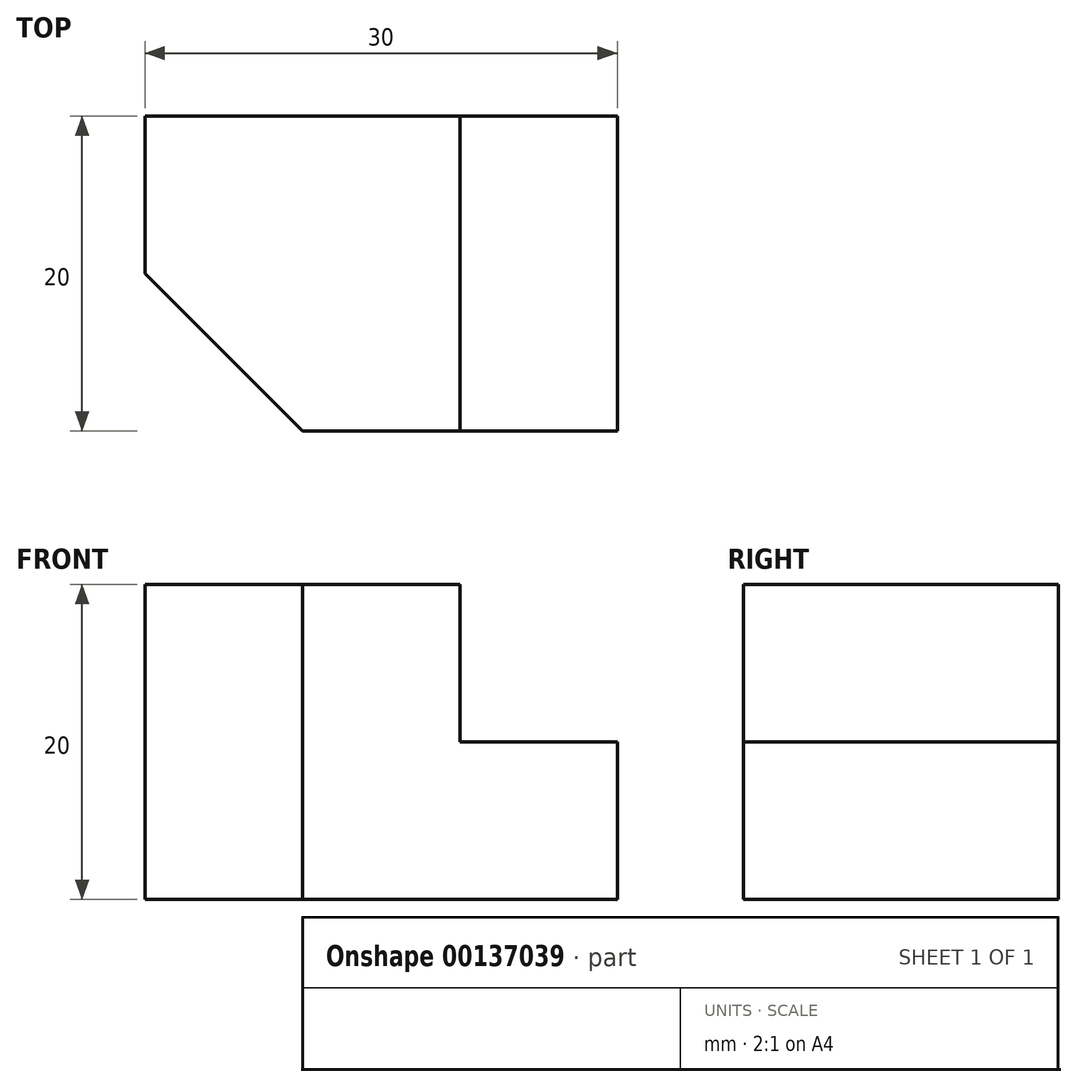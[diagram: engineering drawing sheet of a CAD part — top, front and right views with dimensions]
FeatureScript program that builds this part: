
annotation { "Feature Type Name" : "Feature", "Feature Type Description" : "" }
export const myFeature = defineFeature(function(context is Context, id is Id, definition is map)
    precondition{}
    {
        {
            var Q0;
            Q0=qCreatedBy(makeId("Top.planeOp"),FACE);
            var sketch = newSketch(context, id + "F0", { "sketchPlane" : qUnion([Q0])});
            skLineSegment(sketch, "E0.bottom", {"start": v(0, 0) * mm, "end": v(30, 0) * mm});
            skLineSegment(sketch, "E0.top", {"start": v(0, 20) * mm, "end": v(30, 20) * mm});
            skLineSegment(sketch, "E0.left", {"start": v(0, 0) * mm, "end": v(0, 20) * mm});
            skLineSegment(sketch, "E0.right", {"start": v(30, 0) * mm, "end": v(30, 20) * mm});
            skSolve(sketch);
        }
        {
            var Q0;
            Q0 = qSketchRegion(id + "F0", true);
            extrude(context, id + "F1", {"entities" : qUnion([Q0]), "depth" : 20 * mm});
        }
        {
            var Q0;
            Q0=makeQuery(id+"F1.opExtrude","CAP_FACE",FACE,{"disambiguationData":[OSD([sQuery(id+"F0.wireOp",EDGE,"E0.bottom"),sQuery(id+"F0.wireOp",EDGE,"E0.top"),sQuery(id+"F0.wireOp",EDGE,"E0.left"),sQuery(id+"F0.wireOp",EDGE,"E0.right")])],"isStart":false});
            var sketch = newSketch(context, id + "F2", { "sketchPlane" : qUnion([Q0])});
            skLineSegment(sketch, "E1.bottom", {"start": v(30, 20) * mm, "end": v(20, 20) * mm});
            skLineSegment(sketch, "E1.top", {"start": v(30, 0) * mm, "end": v(20, 0) * mm});
            skLineSegment(sketch, "E1.left", {"start": v(30, 20) * mm, "end": v(30, 0) * mm});
            skLineSegment(sketch, "E1.right", {"start": v(20, 20) * mm, "end": v(20, 0) * mm});
            skSolve(sketch);
        }
        {
            var Q0;
            Q0 = qSketchRegion(id + "F2", true);
            extrude(context, id + "F3", {"entities" : qUnion([Q0]), "operationType" : NewBodyOperationType.REMOVE, "oppositeDirection" : true, "depth" : 10 * mm});
        }
        {
            var Q0;
            Q0=makeQuery(id+"F1.opExtrude","CAP_FACE",FACE,{"disambiguationData":[OSD([sQuery(id+"F0.wireOp",EDGE,"E0.bottom"),sQuery(id+"F0.wireOp",EDGE,"E0.top"),sQuery(id+"F0.wireOp",EDGE,"E0.left"),sQuery(id+"F0.wireOp",EDGE,"E0.right")])],"isStart":false});
            var sketch = newSketch(context, id + "F4", { "sketchPlane" : qUnion([Q0])});
            skLineSegment(sketch, "E2", {"start": v(0, 0) * mm, "end": v(0, 10) * mm});
            skLineSegment(sketch, "E3", {"start": v(0, 10) * mm, "end": v(10, 0) * mm});
            skLineSegment(sketch, "E4", {"start": v(10, 0) * mm, "end": v(0, 0) * mm});
            skSolve(sketch);
        }
        {
            var Q0;
            Q0 = qSketchRegion(id + "F4", true);
            extrude(context, id + "F5", {"entities" : qUnion([Q0]), "operationType" : NewBodyOperationType.REMOVE, "endBound" : BoundingType.THROUGH_ALL, "oppositeDirection" : true, "depth" : 25 * mm});
        }
    });
